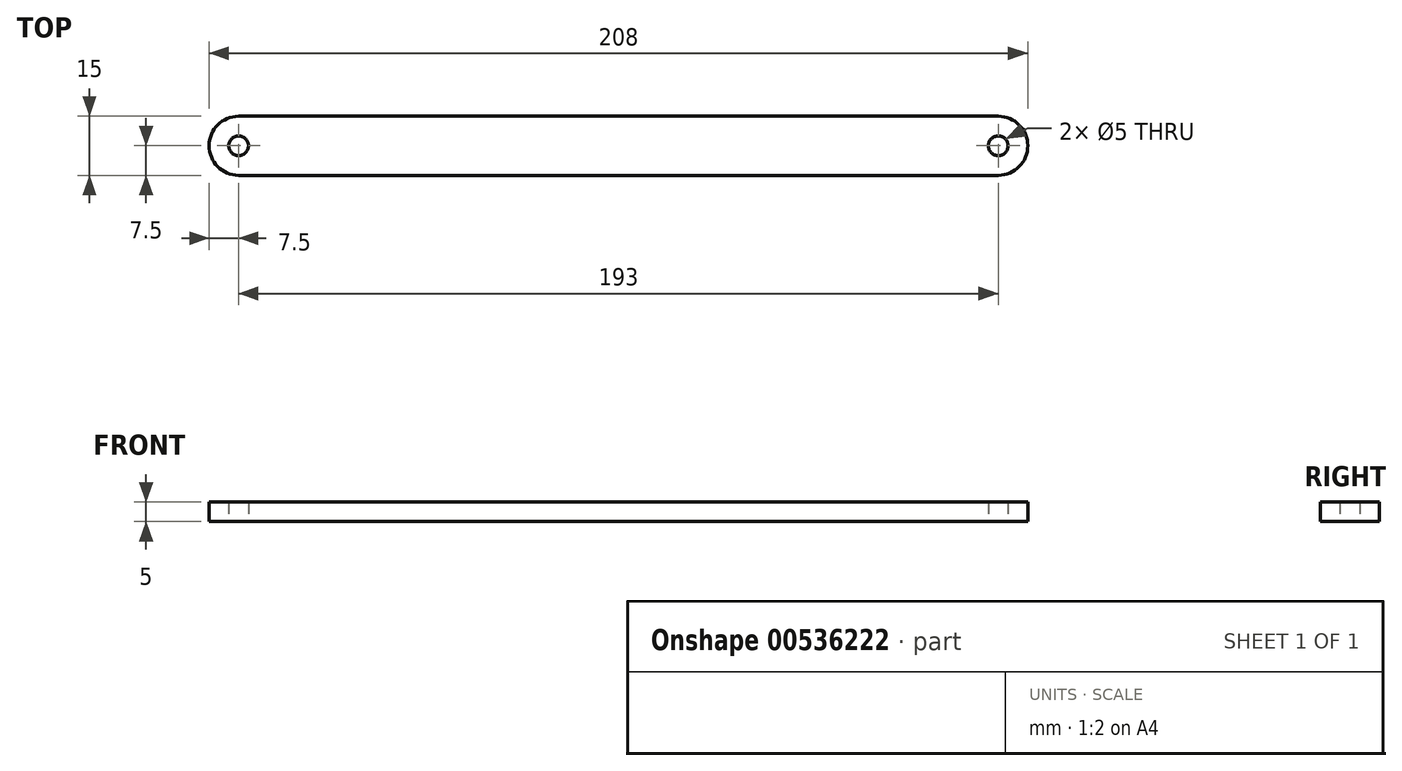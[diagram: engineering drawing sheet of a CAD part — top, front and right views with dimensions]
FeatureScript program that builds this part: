
annotation { "Feature Type Name" : "Feature", "Feature Type Description" : "" }
export const myFeature = defineFeature(function(context is Context, id is Id, definition is map)
    precondition{}
    {
        {
            var Q0;
            Q0=qCreatedBy(makeId("Top.planeOp"),FACE);
            var sketch = newSketch(context, id + "F0", { "sketchPlane" : qUnion([Q0])});
            skLineSegment(sketch, "E0.bottom", {"start": v(193, 7.5) * mm, "end": v(-193, 7.5) * mm});
            skLineSegment(sketch, "E0.top", {"start": v(193, -7.5) * mm, "end": v(-193, -7.5) * mm});
            skPoint(sketch, "E0.middle", {"position": v(0, 0) * mm});
            skArc(sketch, "E1", {"start": v(-193, 7.5) * mm, "mid": v(-200.5, 0) * mm, "end": v(-193, -7.5) * mm});
            skArc(sketch, "E2", {"start": v(193, -7.5) * mm, "mid": v(200.5, 0) * mm, "end": v(193, 7.5) * mm});
            skCircle(sketch, "E3", {"center": v(-193, 0) * mm, "radius": 2.5 * mm});
            skCircle(sketch, "E4", {"center": v(193, 0) * mm, "radius": 2.5 * mm});
            skCircle(sketch, "E5", {"center": v(0, 0) * mm, "radius": 2.5 * mm});
            skSolve(sketch);
        }
        {
            var Q0;
            Q0 = qSketchRegion(id + "F0", true);
            extrude(context, id + "F1", {"entities" : qUnion([Q0]), "depth" : 5 * mm, "offsetDistance" : 25 * mm});
        }
        {
            var Q0;
            Q0=makeQuery(id+"F1.opExtrude","CAP_FACE",FACE,{"disambiguationData":[OSD([sQuery(id+"F0.wireOp",EDGE,"E0.bottom"),sQuery(id+"F0.wireOp",EDGE,"E0.top"),sQuery(id+"F0.wireOp",EDGE,"E1"),sQuery(id+"F0.wireOp",EDGE,"E2"),sQuery(id+"F0.wireOp",EDGE,"E3"),sQuery(id+"F0.wireOp",EDGE,"E4"),sQuery(id+"F0.wireOp",EDGE,"E5")])],"isStart":false});
            var sketch = newSketch(context, id + "F2", { "sketchPlane" : qUnion([Q0])});
            skCircle(sketch, "E6", {"center": v(0, 0) * mm, "radius": 7.5 * mm});
            skSolve(sketch);
        }
        {
            var Q0;
            Q0=makeQuery(id+"F2.imprint","IMPRINT",FACE,{"disambiguationData":[TD([[makeQuery(id+"F2.imprint","IMPRINT",EDGE,{"derivedFrom":makeQuery(id+"F1.opExtrude","CAP_EDGE",EDGE,{"disambiguationData":[OSD([sQuery(id+"F0.wireOp",EDGE,"E5")])],"isStart":false})}),1.0]])]});
            var Q1;
            {var subQ0=makeQuery(id+"F1.opExtrude","CAP_EDGE",EDGE,{"disambiguationData":[OSD([sQuery(id+"F0.wireOp",EDGE,"E2")])],"isStart":false});Q1=makeQuery(id+"F2.imprint","IMPRINT",FACE,{"disambiguationData":[TD([[makeQuery(id+"F2.imprint","IMPRINT",EDGE,{"derivedFrom":subQ0}),1.0]])]});}
            extrude(context, id + "F3", {"entities" : qUnion([Q0, Q1]), "operationType" : NewBodyOperationType.REMOVE, "oppositeDirection" : true, "depth" : 25 * mm, "offsetDistance" : 25 * mm});
        }
    });
